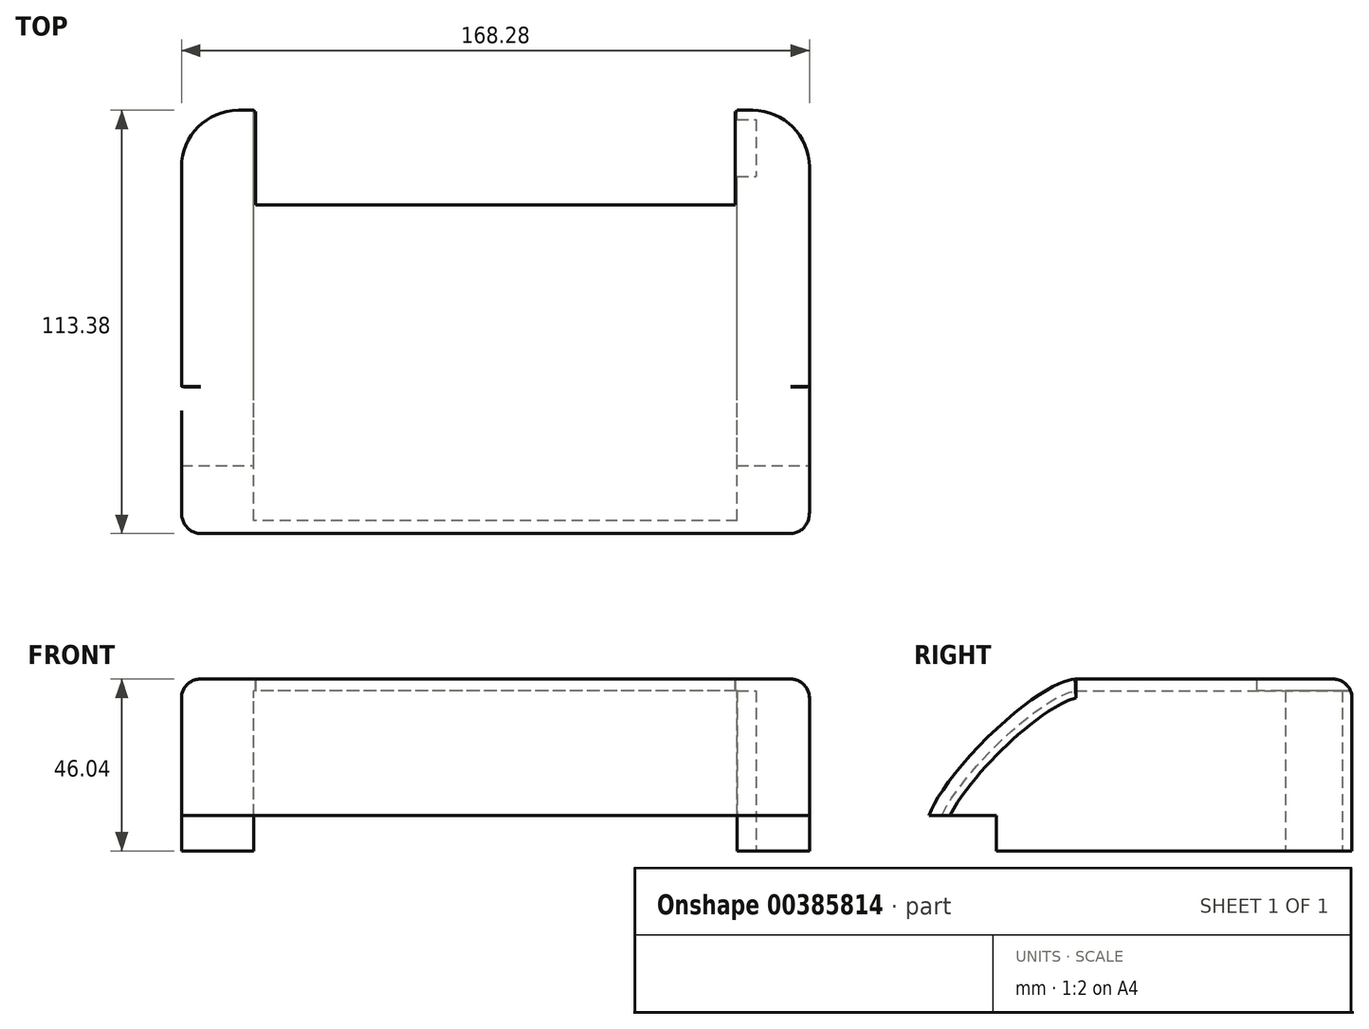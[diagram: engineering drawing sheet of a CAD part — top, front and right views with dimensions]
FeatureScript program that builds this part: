
annotation { "Feature Type Name" : "Feature", "Feature Type Description" : "" }
export const myFeature = defineFeature(function(context is Context, id is Id, definition is map)
    precondition{}
    {
        {
            var Q0;
            Q0=qCreatedBy(makeId("Front.planeOp"),FACE);
            var sketch = newSketch(context, id + "F0", { "sketchPlane" : qUnion([Q0])});
            skLineSegment(sketch, "E0.bottom", {"start": v(-84.14, 46.04) * mm, "end": v(84.14, 46.04) * mm});
            skLineSegment(sketch, "E0.top", {"start": v(-84.14, 0) * mm, "end": v(84.14, 0) * mm});
            skLineSegment(sketch, "E0.left", {"start": v(-84.14, 46.04) * mm, "end": v(-84.14, 0) * mm});
            skLineSegment(sketch, "E0.right", {"start": v(84.14, 46.04) * mm, "end": v(84.14, 0) * mm});
            skSolve(sketch);
        }
        {
            var Q0;
            Q0=makeQuery(id+"F0.imprint","IMPRINT",FACE,{"disambiguationData":[TD([[makeQuery(id+"F0.imprint","IMPRINT",EDGE,{"derivedFrom":sQuery(id+"F0.wireOp",EDGE,"E0.bottom")}),-1.0]])]});
            extrude(context, id + "F1", {"entities" : qUnion([Q0]), "depth" : 114.3 * mm});
        }
        {
            var Q0;
            Q0=makeQuery(id+"F1.opExtrude","CAP_EDGE",EDGE,{"disambiguationData":[OSD([sQuery(id+"F0.wireOp",EDGE,"E0.bottom")])],"isStart":false});
            fillet(context, id + "F2", {"entities" : qUnion([Q0]), "radius" : 40.32 * mm, "tangentPropagation" : true, "rho" : .2, "crossSection" : FilletCrossSection.CONIC, "allowEdgeOverflow" : false});
        }
        {
            var Q0;
            Q0=qCreatedBy(makeId("Right.planeOp"),FACE);
            var sketch = newSketch(context, id + "F3", { "sketchPlane" : qUnion([Q0])});
            skLineSegment(sketch, "E1.0", {"start": v(-73.98, 46.04) * mm, "end": v(0, 46.04) * mm, "construction": true});
            skFitSpline(sketch, "E1.1", {"points": [v(-114.3, 5.72) * mm, v(-114.3, 5.96) * mm, v(-114.27, 6.35) * mm, v(-114.19, 6.9) * mm, v(-114.1, 7.35) * mm, v(-114, 7.74) * mm, v(-113.9, 8.06) * mm, v(-113.83, 8.3) * mm, v(-113.75, 8.55) * mm, v(-113.67, 8.76) * mm, v(-113.61, 8.93) * mm, v(-113.56, 9.07) * mm, v(-113.52, 9.18) * mm, v(-113.5, 9.25) * mm, v(-113.47, 9.3) * mm, v(-113.46, 9.33) * mm, v(-113.45, 9.36) * mm, v(-113.44, 9.39) * mm, v(-113.42, 9.44) * mm, v(-113.38, 9.52) * mm, v(-113.34, 9.62) * mm, v(-113.3, 9.75) * mm, v(-113.22, 9.91) * mm, v(-113.1, 10.18) * mm, v(-112.96, 10.52) * mm, v(-112.76, 10.93) * mm, v(-112.56, 11.35) * mm, v(-112.37, 11.7) * mm, v(-112.22, 12) * mm, v(-112.13, 12.18) * mm, v(-112.05, 12.33) * mm, v(-111.98, 12.44) * mm, v(-111.93, 12.53) * mm, v(-111.9, 12.6) * mm, v(-111.88, 12.64) * mm, v(-111.86, 12.67) * mm, v(-111.85, 12.69) * mm, v(-111.83, 12.72) * mm, v(-111.8, 12.77) * mm, v(-111.76, 12.84) * mm, v(-111.71, 12.93) * mm, v(-111.64, 13.06) * mm, v(-111.56, 13.2) * mm, v(-111.41, 13.45) * mm, v(-111.23, 13.76) * mm, v(-111.01, 14.13) * mm, v(-110.78, 14.5) * mm, v(-110.47, 15) * mm, v(-110.06, 15.64) * mm, v(-109.54, 16.42) * mm, v(-109.08, 17.09) * mm, v(-108.7, 17.62) * mm, v(-108.46, 17.96) * mm, v(-108.26, 18.24) * mm, v(-108.1, 18.44) * mm, v(-107.98, 18.61) * mm, v(-107.9, 18.73) * mm, v(-107.84, 18.8) * mm, v(-107.8, 18.86) * mm, v(-107.77, 18.9) * mm, v(-107.73, 18.96) * mm, v(-107.65, 19.06) * mm, v(-107.54, 19.2) * mm, v(-107.41, 19.38) * mm, v(-107.23, 19.61) * mm, v(-107, 19.9) * mm, v(-106.65, 20.38) * mm, v(-106.18, 20.97) * mm, v(-105.61, 21.68) * mm, v(-105.03, 22.4) * mm, v(-104.53, 23) * mm, v(-104.12, 23.47) * mm, v(-103.81, 23.83) * mm, v(-103.55, 24.14) * mm, v(-103.37, 24.35) * mm, v(-103.26, 24.47) * mm, v(-103.18, 24.56) * mm, v(-103.1, 24.64) * mm, v(-103, 24.76) * mm, v(-102.84, 24.95) * mm, v(-102.59, 25.24) * mm, v(-102.28, 25.57) * mm, v(-101.88, 26.02) * mm, v(-101.37, 26.58) * mm, v(-100.54, 27.47) * mm, v(-99.48, 28.58) * mm, v(-98.18, 29.9) * mm, v(-96.86, 31.2) * mm, v(-95.75, 32.27) * mm, v(-94.85, 33.1) * mm, v(-94.3, 33.6) * mm, v(-93.84, 34.01) * mm, v(-93.5, 34.32) * mm, v(-93.22, 34.57) * mm, v(-93.02, 34.74) * mm, v(-92.9, 34.84) * mm, v(-92.83, 34.92) * mm, v(-92.73, 35) * mm, v(-92.61, 35.1) * mm, v(-92.4, 35.29) * mm, v(-92.1, 35.55) * mm, v(-91.73, 35.86) * mm, v(-91.25, 36.27) * mm, v(-90.65, 36.77) * mm, v(-89.93, 37.36) * mm, v(-89.22, 37.93) * mm, v(-88.62, 38.4) * mm, v(-88.15, 38.76) * mm, v(-87.85, 38.99) * mm, v(-87.62, 39.17) * mm, v(-87.44, 39.3) * mm, v(-87.3, 39.41) * mm, v(-87.2, 39.49) * mm, v(-87.13, 39.53) * mm, v(-87.1, 39.56) * mm, v(-87.04, 39.6) * mm, v(-86.97, 39.65) * mm, v(-86.85, 39.74) * mm, v(-86.68, 39.87) * mm, v(-86.47, 40.02) * mm, v(-86.2, 40.21) * mm, v(-85.86, 40.46) * mm, v(-85.32, 40.83) * mm, v(-84.66, 41.3) * mm, v(-83.88, 41.81) * mm, v(-83.24, 42.22) * mm, v(-82.74, 42.54) * mm, v(-82.36, 42.76) * mm, v(-82, 42.99) * mm, v(-81.69, 43.17) * mm, v(-81.44, 43.3) * mm, v(-81.3, 43.4) * mm, v(-81.17, 43.46) * mm, v(-81.08, 43.51) * mm, v(-81, 43.55) * mm, v(-80.96, 43.58) * mm, v(-80.92, 43.6) * mm, v(-80.9, 43.61) * mm, v(-80.87, 43.63) * mm, v(-80.84, 43.65) * mm, v(-80.77, 43.68) * mm, v(-80.68, 43.74) * mm, v(-80.57, 43.8) * mm, v(-80.42, 43.88) * mm, v(-80.24, 43.97) * mm, v(-79.94, 44.12) * mm, v(-79.59, 44.3) * mm, v(-79.17, 44.51) * mm, v(-78.75, 44.7) * mm, v(-78.42, 44.86) * mm, v(-78.15, 44.97) * mm, v(-77.99, 45.04) * mm, v(-77.86, 45.1) * mm, v(-77.76, 45.13) * mm, v(-77.68, 45.16) * mm, v(-77.63, 45.19) * mm, v(-77.6, 45.2) * mm, v(-77.57, 45.2) * mm, v(-77.54, 45.22) * mm, v(-77.5, 45.24) * mm, v(-77.41, 45.27) * mm, v(-77.3, 45.3) * mm, v(-77.18, 45.36) * mm, v(-77, 45.42) * mm, v(-76.8, 45.5) * mm, v(-76.54, 45.57) * mm, v(-76.3, 45.65) * mm, v(-75.99, 45.74) * mm, v(-75.6, 45.83) * mm, v(-75.16, 45.93) * mm, v(-74.6, 46.01) * mm, v(-74.22, 46.04) * mm, v(-73.98, 46.04) * mm], "construction": true});
            skLineSegment(sketch, "E1.2", {"start": v(-114.3, 5.72) * mm, "end": v(-114.3, 0) * mm, "construction": true});
            skLineSegment(sketch, "E2.0", {"start": v(-73.98, 42.86) * mm, "end": v(0, 42.86) * mm});
            skFitSpline(sketch, "E2.1", {"points": [v(-111.13, 5.72) * mm, v(-111.13, 5.8) * mm, v(-111.11, 6) * mm, v(-111.06, 6.33) * mm, v(-111, 6.63) * mm, v(-110.92, 6.96) * mm, v(-110.82, 7.27) * mm, v(-110.74, 7.53) * mm, v(-110.68, 7.7) * mm, v(-110.63, 7.85) * mm, v(-110.59, 7.95) * mm, v(-110.55, 8.04) * mm, v(-110.53, 8.11) * mm, v(-110.51, 8.15) * mm, v(-110.5, 8.18) * mm, v(-110.5, 8.2) * mm, v(-110.48, 8.22) * mm, v(-110.47, 8.27) * mm, v(-110.44, 8.34) * mm, v(-110.4, 8.42) * mm, v(-110.36, 8.53) * mm, v(-110.3, 8.67) * mm, v(-110.2, 8.9) * mm, v(-110.07, 9.2) * mm, v(-109.9, 9.55) * mm, v(-109.72, 9.93) * mm, v(-109.55, 10.25) * mm, v(-109.41, 10.52) * mm, v(-109.33, 10.68) * mm, v(-109.25, 10.82) * mm, v(-109.2, 10.92) * mm, v(-109.15, 11) * mm, v(-109.12, 11.07) * mm, v(-109.1, 11.1) * mm, v(-109.08, 11.13) * mm, v(-109.07, 11.14) * mm, v(-109.06, 11.17) * mm, v(-109.03, 11.22) * mm, v(-109, 11.3) * mm, v(-108.95, 11.37) * mm, v(-108.88, 11.48) * mm, v(-108.8, 11.62) * mm, v(-108.67, 11.85) * mm, v(-108.5, 12.13) * mm, v(-108.3, 12.48) * mm, v(-108.08, 12.83) * mm, v(-107.79, 13.3) * mm, v(-107.4, 13.9) * mm, v(-106.9, 14.64) * mm, v(-106.47, 15.27) * mm, v(-106.11, 15.78) * mm, v(-105.88, 16.1) * mm, v(-105.7, 16.37) * mm, v(-105.55, 16.56) * mm, v(-105.43, 16.73) * mm, v(-105.34, 16.85) * mm, v(-105.3, 16.91) * mm, v(-105.25, 16.96) * mm, v(-105.23, 17) * mm, v(-105.18, 17.06) * mm, v(-105.11, 17.16) * mm, v(-105, 17.3) * mm, v(-104.88, 17.47) * mm, v(-104.7, 17.7) * mm, v(-104.5, 17.97) * mm, v(-104.14, 18.43) * mm, v(-103.7, 19) * mm, v(-103.15, 19.68) * mm, v(-102.58, 20.37) * mm, v(-102.1, 20.95) * mm, v(-101.7, 21.41) * mm, v(-101.4, 21.76) * mm, v(-101.15, 22.06) * mm, v(-100.97, 22.26) * mm, v(-100.87, 22.38) * mm, v(-100.8, 22.47) * mm, v(-100.72, 22.55) * mm, v(-100.63, 22.66) * mm, v(-100.46, 22.85) * mm, v(-100.21, 23.12) * mm, v(-99.92, 23.45) * mm, v(-99.53, 23.89) * mm, v(-99.03, 24.43) * mm, v(-98.23, 25.3) * mm, v(-97.2, 26.37) * mm, v(-95.94, 27.66) * mm, v(-94.65, 28.93) * mm, v(-93.57, 29.95) * mm, v(-92.7, 30.76) * mm, v(-92.16, 31.26) * mm, v(-91.72, 31.65) * mm, v(-91.4, 31.95) * mm, v(-91.12, 32.2) * mm, v(-90.93, 32.36) * mm, v(-90.82, 32.46) * mm, v(-90.74, 32.53) * mm, v(-90.64, 32.6) * mm, v(-90.53, 32.7) * mm, v(-90.32, 32.89) * mm, v(-90.03, 33.14) * mm, v(-89.68, 33.44) * mm, v(-89.2, 33.84) * mm, v(-88.63, 34.32) * mm, v(-87.93, 34.9) * mm, v(-87.24, 35.45) * mm, v(-86.67, 35.9) * mm, v(-86.22, 36.25) * mm, v(-85.93, 36.46) * mm, v(-85.7, 36.63) * mm, v(-85.54, 36.76) * mm, v(-85.4, 36.87) * mm, v(-85.3, 36.94) * mm, v(-85.24, 36.98) * mm, v(-85.2, 37.01) * mm, v(-85.15, 37.05) * mm, v(-85.08, 37.1) * mm, v(-84.97, 37.18) * mm, v(-84.8, 37.3) * mm, v(-84.6, 37.45) * mm, v(-84.34, 37.64) * mm, v(-84.02, 37.87) * mm, v(-83.5, 38.23) * mm, v(-82.88, 38.66) * mm, v(-82.14, 39.15) * mm, v(-81.54, 39.54) * mm, v(-81.07, 39.84) * mm, v(-80.72, 40.05) * mm, v(-80.37, 40.26) * mm, v(-80.09, 40.42) * mm, v(-79.86, 40.55) * mm, v(-79.72, 40.63) * mm, v(-79.61, 40.7) * mm, v(-79.53, 40.74) * mm, v(-79.46, 40.78) * mm, v(-79.41, 40.8) * mm, v(-79.38, 40.82) * mm, v(-79.37, 40.83) * mm, v(-79.34, 40.85) * mm, v(-79.3, 40.87) * mm, v(-79.24, 40.9) * mm, v(-79.16, 40.95) * mm, v(-79.06, 41) * mm, v(-78.92, 41.08) * mm, v(-78.76, 41.16) * mm, v(-78.5, 41.3) * mm, v(-78.17, 41.47) * mm, v(-77.8, 41.65) * mm, v(-77.43, 41.82) * mm, v(-77.14, 41.95) * mm, v(-76.91, 42.05) * mm, v(-76.77, 42.1) * mm, v(-76.66, 42.15) * mm, v(-76.58, 42.18) * mm, v(-76.5, 42.21) * mm, v(-76.46, 42.23) * mm, v(-76.43, 42.24) * mm, v(-76.42, 42.25) * mm, v(-76.39, 42.26) * mm, v(-76.35, 42.27) * mm, v(-76.29, 42.3) * mm, v(-76.2, 42.33) * mm, v(-76.09, 42.37) * mm, v(-75.95, 42.42) * mm, v(-75.78, 42.48) * mm, v(-75.52, 42.57) * mm, v(-75.21, 42.66) * mm, v(-74.88, 42.74) * mm, v(-74.6, 42.8) * mm, v(-74.26, 42.85) * mm, v(-74.07, 42.86) * mm, v(-73.98, 42.86) * mm]});
            skLineSegment(sketch, "E2.2", {"start": v(-111.13, 5.72) * mm, "end": v(-111.13, 0) * mm});
            skLineSegment(sketch, "E3", {"start": v(-111.13, 0) * mm, "end": v(0, 0) * mm});
            skLineSegment(sketch, "E4", {"start": v(0, 0) * mm, "end": v(0, 42.86) * mm});
            skSolve(sketch);
        }
        {
            var Q0;
            Q0 = qSketchRegion(id + "F3", true);
            extrude(context, id + "F4", {"entities" : qUnion([Q0]), "operationType" : NewBodyOperationType.REMOVE, "endBound" : BoundingType.SYMMETRIC, "depth" : 129.54 * mm});
        }
        {
            var Q0;
            Q0=makeQuery(id+"F1.opExtrude","CAP_EDGE",EDGE,{"disambiguationData":[OSD([sQuery(id+"F0.wireOp",EDGE,"E0.right")])],"isStart":true});
            var Q1;
            Q1=makeQuery(id+"F1.opExtrude","CAP_EDGE",EDGE,{"disambiguationData":[OSD([sQuery(id+"F0.wireOp",EDGE,"E0.left")])],"isStart":true});
            fillet(context, id + "F5", {"entities" : qUnion([Q0, Q1]), "radius" : 15.24 * mm, "tangentPropagation" : true, "allowEdgeOverflow" : false});
        }
        {
            var Q0;
            Q0=makeQuery(id+"F1.opExtrude","SWEPT_FACE",FACE,{"disambiguationData":[OSD([sQuery(id+"F0.wireOp",EDGE,"E0.right")])]});
            var sketch = newSketch(context, id + "F6", { "sketchPlane" : qUnion([Q0])});
            skLineSegment(sketch, "E5.bottom", {"start": v(-114.3, 0) * mm, "end": v(-95.25, 0) * mm});
            skLineSegment(sketch, "E5.top", {"start": v(-114.3, 9.53) * mm, "end": v(-95.25, 9.53) * mm});
            skLineSegment(sketch, "E5.left", {"start": v(-114.3, 0) * mm, "end": v(-114.3, 9.53) * mm});
            skLineSegment(sketch, "E5.right", {"start": v(-95.25, 0) * mm, "end": v(-95.25, 9.53) * mm});
            skSolve(sketch);
        }
        {
            var Q0;
            Q0 = qSketchRegion(id + "F6", true);
            extrude(context, id + "F7", {"entities" : qUnion([Q0]), "operationType" : NewBodyOperationType.REMOVE, "endBound" : BoundingType.THROUGH_ALL, "oppositeDirection" : true, "depth" : 25.4 * mm});
        }
        {
            var Q0;
            Q0=makeQuery(id+"F1.opExtrude","SWEPT_EDGE",EDGE,{"disambiguationData":[OSD([sQuery(id+"F0.wireOp",EDGE,"E0.bottom"),sQuery(id+"F0.wireOp",EDGE,"E0.right")])]});
            fillet(context, id + "F8", {"entities" : qUnion([Q0]), "radius" : 5.08 * mm, "tangentPropagation" : true, "allowEdgeOverflow" : false});
        }
        {
            var Q0;
            Q0=makeQuery(id+"F8.opFillet","SPLIT",FACE,{"disambiguationData":[OD(1.0)],"derivedFrom":makeQuery(id+"F1.opExtrude","CAP_FACE",FACE,{"disambiguationData":[OSD([sQuery(id+"F0.wireOp",EDGE,"E0.bottom"),sQuery(id+"F0.wireOp",EDGE,"E0.top"),sQuery(id+"F0.wireOp",EDGE,"E0.left"),sQuery(id+"F0.wireOp",EDGE,"E0.right")])],"isStart":true})});
            var sketch = newSketch(context, id + "F9", { "sketchPlane" : qUnion([Q0])});
            skLineSegment(sketch, "E6.bottom", {"start": v(-64.3, 40.96) * mm, "end": v(64.3, 40.96) * mm});
            skLineSegment(sketch, "E6.top", {"start": v(-64.3, 46.04) * mm, "end": v(64.3, 46.04) * mm});
            skLineSegment(sketch, "E6.left", {"start": v(-64.3, 40.96) * mm, "end": v(-64.3, 46.04) * mm});
            skLineSegment(sketch, "E6.right", {"start": v(64.3, 40.96) * mm, "end": v(64.3, 46.04) * mm});
            skLineSegment(sketch, "E7.0", {"start": v(-68.9, 46.04) * mm, "end": v(68.9, 46.04) * mm, "construction": true});
            skSolve(sketch);
        }
        {
            var Q0;
            Q0 = qSketchRegion(id + "F9", true);
            extrude(context, id + "F10", {"entities" : qUnion([Q0]), "operationType" : NewBodyOperationType.REMOVE, "oppositeDirection" : true, "depth" : 25.4 * mm});
        }
        {
            var Q0;
            {var subQ0=sQuery(id+"F0.wireOp",EDGE,"E0.right");var subQ1=sQuery(id+"F0.wireOp",EDGE,"E0.top");Q0=makeQuery(id+"F7.boolean.opBoolean","SPLIT",FACE,{"disambiguationData":[TD([makeQuery(id+"F1.opExtrude","SWEPT_FACE",FACE,{"disambiguationData":[OSD([subQ0])]})])],"derivedFrom":makeQuery(id+"F1.opExtrude","SWEPT_FACE",FACE,{"disambiguationData":[OSD([subQ1])]})});}
            var sketch = newSketch(context, id + "F11", { "sketchPlane" : qUnion([Q0])});
            skLineSegment(sketch, "E8.bottom", {"start": v(64.77, 2.54) * mm, "end": v(69.85, 2.54) * mm});
            skLineSegment(sketch, "E8.top", {"start": v(64.77, 17.78) * mm, "end": v(69.85, 17.78) * mm});
            skLineSegment(sketch, "E8.left", {"start": v(64.77, 2.54) * mm, "end": v(64.77, 17.78) * mm});
            skLineSegment(sketch, "E8.right", {"start": v(69.85, 2.54) * mm, "end": v(69.85, 17.78) * mm});
            skSolve(sketch);
        }
        {
            var Q0;
            Q0=makeQuery(id+"F11.imprint","IMPRINT",FACE,{"disambiguationData":[TD([[makeQuery(id+"F11.imprint","IMPRINT",EDGE,{"derivedFrom":sQuery(id+"F11.wireOp",EDGE,"E8.bottom")}),1.0]])]});
            var Q1;
            Q1=makeQuery(id+"F4.boolean.opBoolean","COPY",FACE,{"derivedFrom":makeQuery(id+"F4.opExtrude","SWEPT_FACE",FACE,{"disambiguationData":[OSD([sQuery(id+"F3.wireOp",EDGE,"E2.0")])]})});
            extrude(context, id + "F12", {"entities" : qUnion([Q0]), "operationType" : NewBodyOperationType.REMOVE, "endBound" : BoundingType.UP_TO_SURFACE, "oppositeDirection" : true, "endBoundEntityFace" : qUnion([Q1]), "depth" : 25.4 * mm});
        }
    });
